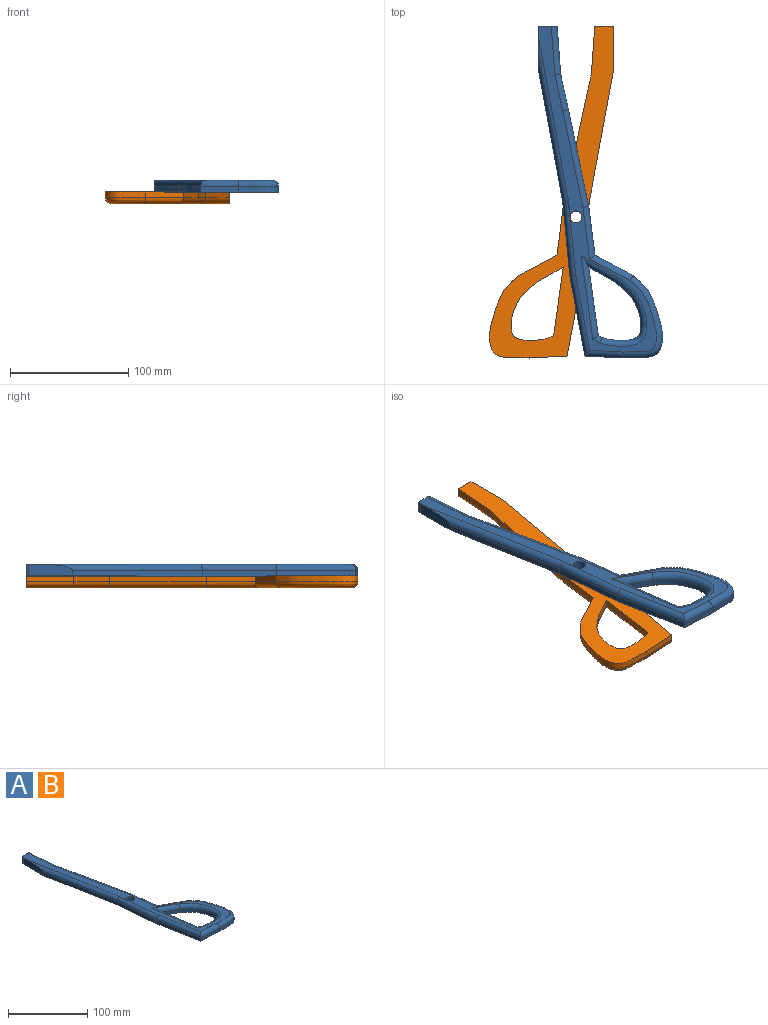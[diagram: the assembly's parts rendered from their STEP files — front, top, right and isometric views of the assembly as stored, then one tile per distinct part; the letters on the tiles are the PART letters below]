
ASSEMBLY  parts=2 mates=1
PART A: 34 faces, bbox 114.6x286.3x14.2 mm
  f0: plane 57.85x8.08mm, normal (0.99,0.14,0), area 292mm2, adj f1,f16,f18,f20
  f1: plane 21.73x12.45mm, normal (-0.5,-0.87,0), area 125.2mm2, adj f0,f2,f18,f21
  f2: extruded ~49.57x32.89mm, area 431.2mm2, adj f1,f16,f18,f23
  f3: plane 15.69x10.15mm, normal (0,1,0), area 150mm2, adj f4,f15,f17,f18,f33
  f4: plane 10x2.47mm, normal (-1,0,0), area 24.7mm2, adj f3,f5,f17,f18
  f5: plane 40.8x14.23mm, normal (-1,0,0), area 335.9mm2, adj f4,f6,f17,f18,f24
  f6: plane 110.03x20.22mm, normal (-0.98,-0.18,0), area 559.4mm2, adj f5,f7,f18,f24
  f7: plane 62.96x6.01mm, normal (-1,-0.09,0), area 316.2mm2, adj f6,f8,f18,f25
  f8: plane 67.29x12.67mm, normal (-0.98,-0.18,0), area 342.4mm2, adj f7,f9,f18,f26
  f9: plane 32.22x5mm, normal (-0.05,-1,0), area 161.4mm2, adj f8,f10,f18,f27
  f10: extruded ~69.62x33.64mm, area 519.7mm2, adj f9,f11,f18,f28
  f11: plane 32.5x17.28mm, normal (0.47,0.88,0), area 184mm2, adj f10,f12,f18,f29
  f12: plane 41.55x5.32mm, normal (0.99,0.13,0), area 209.4mm2, adj f11,f13,f18,f30
  f13: plane 81.85x17.23mm, normal (0.98,0.21,0), area 418.2mm2, adj f12,f14,f18,f31
  f14: plane 30.18x6.57mm, normal (0.98,0.21,0), area 154.4mm2, adj f13,f15,f18,f32
  f15: plane 40.58x5mm, normal (1,0.07,0), area 203.4mm2, adj f3,f14,f18,f33
  f16: plane 5x3.13mm, normal (0.47,0.88,0), area 17.7mm2, adj f0,f2,f18,f22
  f17: plane 276.04x99.76mm, normal (0,0,1), area 3135mm2, adj f3,f4,f5,f19,f20,f21,f22,f23
  f18: plane 281.71x105.42mm, normal (0,0,-1), area 7201.4mm2, adj f0,f1,f2,f3,f4,f5,f6,f7
  f19: cylinder r=5.04mm len=10.08mm, axis (0,0,1), area 316.8mm2, adj f17,f18,f25
  f20: cylinder r=5mm len=71.17mm, axis (0.14,-0.99,0), area 508.8mm2, adj f0,f17,f21,f22
  f21: cylinder r=5mm len=33.51mm, axis (-0.87,0.5,0), area 238.8mm2, adj f1,f17,f20,f23
  f22: cylinder r=5mm len=7.99mm, axis (0.88,-0.47,0), area 39mm2, adj f16,f17,f20,f23
  f23: bspline ~59.17x40.28mm, area 720.9mm2, adj f2,f17,f21,f22
  f24: cylinder r=5mm len=137.89mm, axis (-0.18,0.98,0), area 986.3mm2, adj f5,f6,f17,f25
  f25: cylinder r=5mm len=63.65mm, axis (-0.09,1,0), area 496.7mm2, adj f7,f17,f19,f24,f26
  f26: cylinder r=5mm len=68.21mm, axis (-0.18,0.98,0), area 521.5mm2, adj f8,f17,f25,f27
  f27: cylinder r=5mm len=32.49mm, axis (-1,0.05,0), area 236.7mm2, adj f9,f17,f26,f28
  f28: bspline ~69.73x34.52mm, area 779.1mm2, adj f10,f17,f27,f29
  f29: cylinder r=5mm len=37.13mm, axis (0.88,-0.47,0), area 297.3mm2, adj f11,f17,f28,f30
  f30: cylinder r=5mm len=44.75mm, axis (0.13,-0.99,0), area 338.3mm2, adj f12,f17,f29,f31
  f31: cylinder r=5mm len=82.88mm, axis (0.21,-0.98,0), area 656mm2, adj f13,f17,f30,f32
  f32: cylinder r=5mm len=31.59mm, axis (0.21,-0.98,0), area 243.9mm2, adj f14,f17,f31,f33
  f33: cylinder r=5mm len=41.65mm, axis (0.07,-1,0), area 322.3mm2, adj f3,f15,f17,f32
PART B: same geometry as A
PLACE A rot(axis=(0,1,0),0deg) t=(3.38,-15.21,-21.43)mm
PLACE B rot(axis=(0,-1,0),180deg) t=(3.38,-15.21,-21.43)mm
MATE revolute A.f19 <-> B.f19  axis (0,0,-1) through (3.38,-15.21,-21.43)mm
